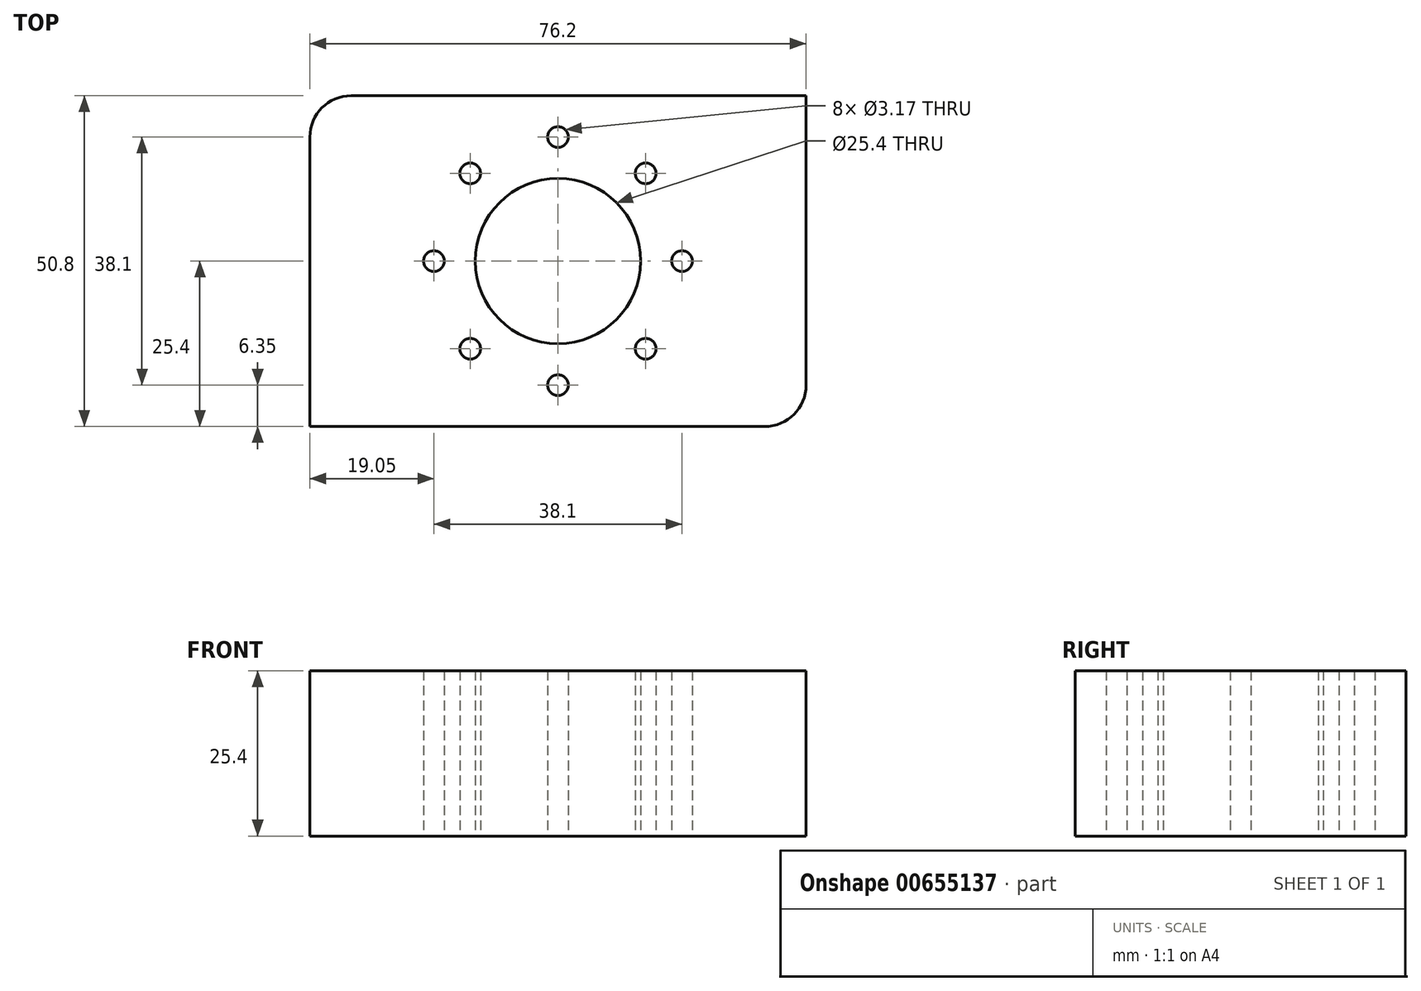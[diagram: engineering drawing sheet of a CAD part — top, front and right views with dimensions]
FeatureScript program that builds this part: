
annotation { "Feature Type Name" : "Feature", "Feature Type Description" : "" }
export const myFeature = defineFeature(function(context is Context, id is Id, definition is map)
    precondition{}
    {
        {
            var Q0;
            Q0=qCreatedBy(makeId("Top.planeOp"),FACE);
            var sketch = newSketch(context, id + "F0", { "sketchPlane" : qUnion([Q0])});
            skLineSegment(sketch, "E0.bottom", {"start": v(38.1, 25.4) * mm, "end": v(-31.75, 25.4) * mm});
            skLineSegment(sketch, "E0.top", {"start": v(31.75, -25.4) * mm, "end": v(-38.1, -25.4) * mm});
            skLineSegment(sketch, "E0.left", {"start": v(38.1, 25.4) * mm, "end": v(38.1, -19.05) * mm});
            skLineSegment(sketch, "E0.right", {"start": v(-38.1, 19.05) * mm, "end": v(-38.1, -25.4) * mm});
            skPoint(sketch, "E0.middle", {"position": v(0, 0) * mm});
            skCircle(sketch, "E1", {"center": v(0, 0) * mm, "radius": 12.7 * mm});
            skPoint(sketch, "E2.visualSharp", {"position": v(-38.1, 25.4) * mm});
            skArc(sketch, "E2.filletArc", {"start": v(-31.75, 25.4) * mm, "mid": v(-36.24, 23.54) * mm, "end": v(-38.1, 19.05) * mm});
            skPoint(sketch, "E3.visualSharp", {"position": v(38.1, -25.4) * mm});
            skArc(sketch, "E3.filletArc", {"start": v(31.75, -25.4) * mm, "mid": v(36.24, -23.54) * mm, "end": v(38.1, -19.05) * mm});
            skCircle(sketch, "E4", {"center": v(-19.05, 0) * mm, "radius": 1.59 * mm});
            skCircle(sketch, "E5.1.0", {"center": v(-13.47, -13.47) * mm, "radius": 1.59 * mm});
            skCircle(sketch, "E5.2.0", {"center": v(0, -19.05) * mm, "radius": 1.59 * mm});
            skCircle(sketch, "E5.3.0", {"center": v(13.47, -13.47) * mm, "radius": 1.59 * mm});
            skCircle(sketch, "E5.4.0", {"center": v(19.05, 0) * mm, "radius": 1.59 * mm});
            skCircle(sketch, "E5.5.0", {"center": v(13.47, 13.47) * mm, "radius": 1.59 * mm});
            skCircle(sketch, "E5.6.0", {"center": v(0, 19.05) * mm, "radius": 1.59 * mm});
            skCircle(sketch, "E5.7.0", {"center": v(-13.47, 13.47) * mm, "radius": 1.59 * mm});
            skSolve(sketch);
        }
        {
            var Q0;
            Q0=makeQuery(id+"F0.imprint","IMPRINT",FACE,{"disambiguationData":[TD([[makeQuery(id+"F0.imprint","IMPRINT",EDGE,{"derivedFrom":sQuery(id+"F0.wireOp",EDGE,"E0.bottom")}),1.0]])]});
            extrude(context, id + "F1", {"entities" : qUnion([Q0]), "depth" : 25.4 * mm, "offsetDistance" : 25.4 * mm});
        }
    });
